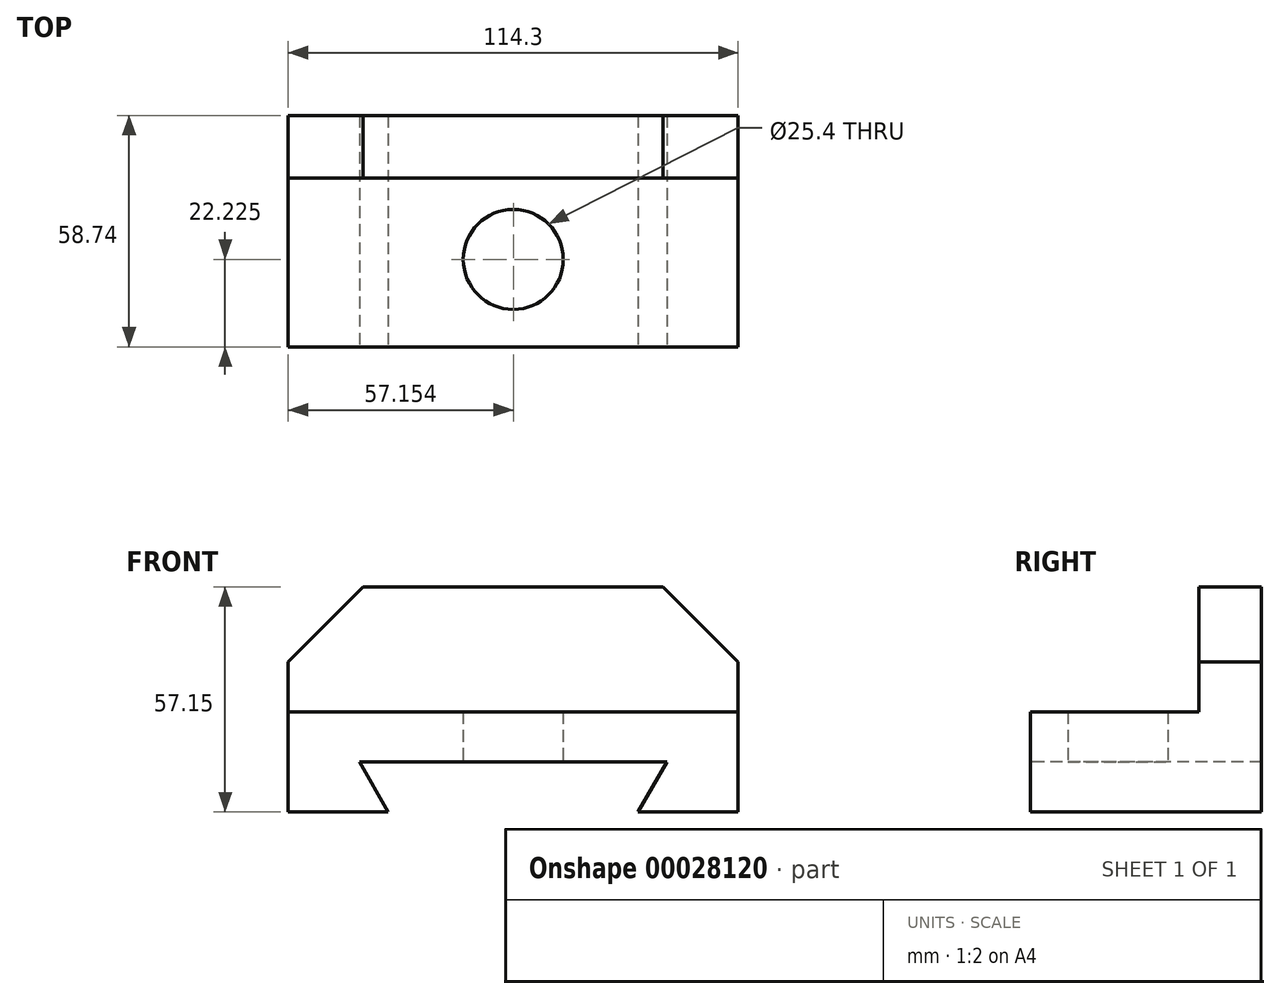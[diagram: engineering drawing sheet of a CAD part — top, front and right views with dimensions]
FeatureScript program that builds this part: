
annotation { "Feature Type Name" : "Feature", "Feature Type Description" : "" }
export const myFeature = defineFeature(function(context is Context, id is Id, definition is map)
    precondition{}
    {
        {
            var Q0;
            Q0=qCreatedBy(makeId("Top.planeOp"),FACE);
            var sketch = newSketch(context, id + "F0", { "sketchPlane" : qUnion([Q0])});
            skLineSegment(sketch, "E0.bottom", {"start": v(-98.54, 40.5) * mm, "end": v(15.76, 40.5) * mm});
            skLineSegment(sketch, "E0.top", {"start": v(-98.54, -18.23) * mm, "end": v(15.76, -18.23) * mm});
            skLineSegment(sketch, "E0.left", {"start": v(-98.54, 40.5) * mm, "end": v(-98.54, -18.23) * mm});
            skLineSegment(sketch, "E0.right", {"start": v(15.76, 40.5) * mm, "end": v(15.76, -18.23) * mm});
            skLineSegment(sketch, "E1.top", {"start": v(-98.54, 24.63) * mm, "end": v(15.76, 24.63) * mm});
            skLineSegment(sketch, "E1.left", {"start": v(-98.54, 40.5) * mm, "end": v(-98.54, 24.63) * mm});
            skLineSegment(sketch, "E1.right", {"start": v(15.76, 40.5) * mm, "end": v(15.76, 24.63) * mm});
            skCircle(sketch, "E2", {"center": v(-41.39, 4) * mm, "radius": 12.7 * mm});
            skSolve(sketch);
        }
        {
            var Q0;
            Q0=makeQuery(id+"F0.imprint","IMPRINT",FACE,{"disambiguationData":[TD([[makeQuery(id+"F0.imprint","IMPRINT",EDGE,{"derivedFrom":sQuery(id+"F0.wireOp",EDGE,"E0.bottom")}),-1.0]])]});
            var Q1;
            Q1=makeQuery(id+"F0.imprint","IMPRINT",FACE,{"disambiguationData":[TD([[makeQuery(id+"F0.imprint","IMPRINT",EDGE,{"derivedFrom":sQuery(id+"F0.wireOp",EDGE,"E0.top")}),1.0]])]});
            extrude(context, id + "F1", {"entities" : qUnion([Q0, Q1]), "depth" : 25.4 * mm});
        }
        {
            var Q0;
            Q0=makeQuery(id+"F1.opExtrude","SWEPT_FACE",FACE,{"disambiguationData":[OSD([sQuery(id+"F0.wireOp",EDGE,"E0.top")])]});
            var sketch = newSketch(context, id + "F2", { "sketchPlane" : qUnion([Q0])});
            skLineSegment(sketch, "E3", {"start": v(-73.14, 0) * mm, "end": v(-80.47, 12.7) * mm});
            skLineSegment(sketch, "E4", {"start": v(-80.47, 12.7) * mm, "end": v(-2.3, 12.7) * mm});
            skLineSegment(sketch, "E5", {"start": v(-2.3, 12.7) * mm, "end": v(-9.64, 0) * mm});
            skSolve(sketch);
        }
        {
            var Q0;
            Q0 = qSketchRegion(id + "F2", true);
            var Q1;
            {var subQ2=sQuery(id+"F2.wireOp",EDGE,"E3");Q1=makeQuery(id+"F2.imprint","IMPRINT",FACE,{"disambiguationData":[TD([[makeQuery(id+"F2.imprint","IMPRINT",EDGE,{"derivedFrom":subQ2}),-1.0]])]});}
            extrude(context, id + "F3", {"entities" : qUnion([Q0, Q1]), "operationType" : NewBodyOperationType.REMOVE, "endBound" : BoundingType.THROUGH_ALL, "oppositeDirection" : true, "depth" : 25.4 * mm});
        }
        {
            var Q0;
            Q0=makeQuery(id+"F1.opExtrude","CAP_FACE",FACE,{"disambiguationData":[OSD([sQuery(id+"F0.wireOp",EDGE,"E0.top"),sQuery(id+"F0.wireOp",EDGE,"E0.left"),sQuery(id+"F0.wireOp",EDGE,"E0.right"),sQuery(id+"F0.wireOp",EDGE,"E0.bottom"),sQuery(id+"F0.wireOp",EDGE,"E1.left"),sQuery(id+"F0.wireOp",EDGE,"E1.right"),sQuery(id+"F0.wireOp",EDGE,"E2")])],"isStart":false});
            var sketch = newSketch(context, id + "F4", { "sketchPlane" : qUnion([Q0])});
            skLineSegment(sketch, "E6.0", {"start": v(-98.54, 24.63) * mm, "end": v(15.76, 24.63) * mm});
            skSolve(sketch);
        }
        {
            var Q0;
            {var subQ1=sQuery(id+"F4.wireOp",EDGE,"E6.0");Q0=makeQuery(id+"F4.imprint","IMPRINT",FACE,{"disambiguationData":[TD([[makeQuery(id+"F4.imprint","IMPRINT",EDGE,{"derivedFrom":subQ1}),1.0]])]});}
            extrude(context, id + "F5", {"entities" : qUnion([Q0]), "operationType" : NewBodyOperationType.ADD, "depth" : 31.75 * mm});
        }
        {
            var Q0;
            Q0=makeQuery(id+"F5.opExtrude","CAP_EDGE",EDGE,{"disambiguationData":[OSD([sQuery(id+"F0.wireOp",EDGE,"E0.left"),sQuery(id+"F0.wireOp",EDGE,"E1.left")])],"isStart":false});
            var Q1;
            Q1=makeQuery(id+"F5.opExtrude","CAP_EDGE",EDGE,{"disambiguationData":[OSD([sQuery(id+"F0.wireOp",EDGE,"E0.right"),sQuery(id+"F0.wireOp",EDGE,"E1.right")])],"isStart":false});
            chamfer(context, id + "F6", {"entities" : qUnion([Q0, Q1]), "width" : 19.05 * mm, "tangentPropagation" : true});
        }
    });
